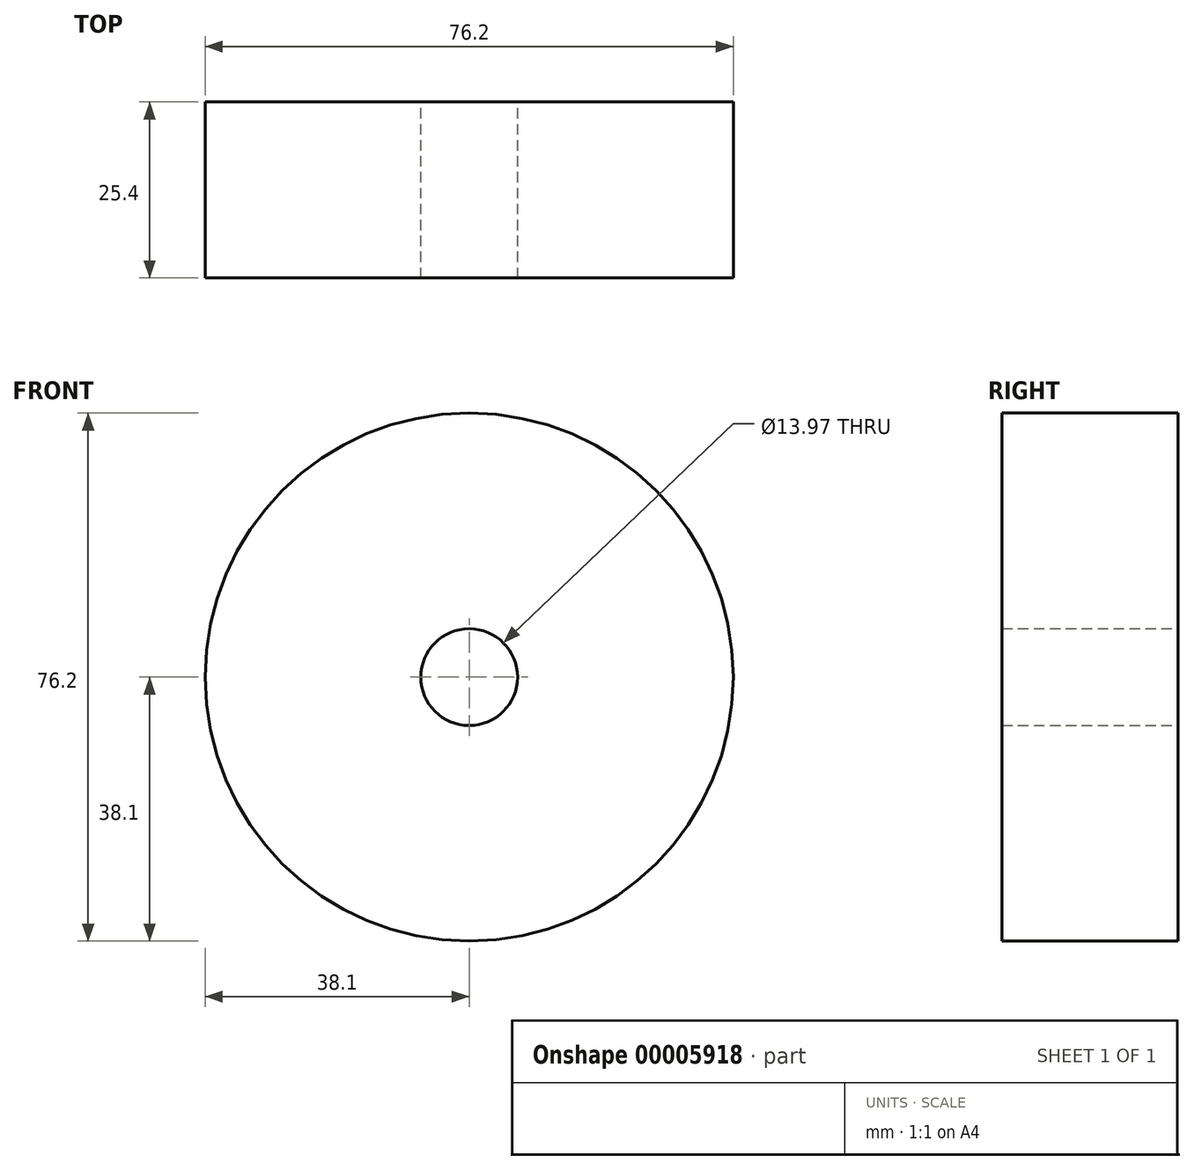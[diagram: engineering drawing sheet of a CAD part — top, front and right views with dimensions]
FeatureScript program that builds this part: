
annotation { "Feature Type Name" : "Feature", "Feature Type Description" : "" }
export const myFeature = defineFeature(function(context is Context, id is Id, definition is map)
    precondition{}
    {
        {
            var Q0;
            Q0=qCreatedBy(makeId("Front.planeOp"),FACE);
            var sketch = newSketch(context, id + "F0", { "sketchPlane" : qUnion([Q0])});
            skCircle(sketch, "E0", {"center": v(0, 0) * mm, "radius": 38.1 * mm});
            skCircle(sketch, "E1", {"center": v(0, 0) * mm, "radius": 6.99 * mm});
            skSolve(sketch);
        }
        {
            var Q0;
            Q0 = qSketchRegion(id + "F0", true);
            extrude(context, id + "F1", {"entities" : qUnion([Q0]), "depth" : 25.4 * mm});
        }
    });
